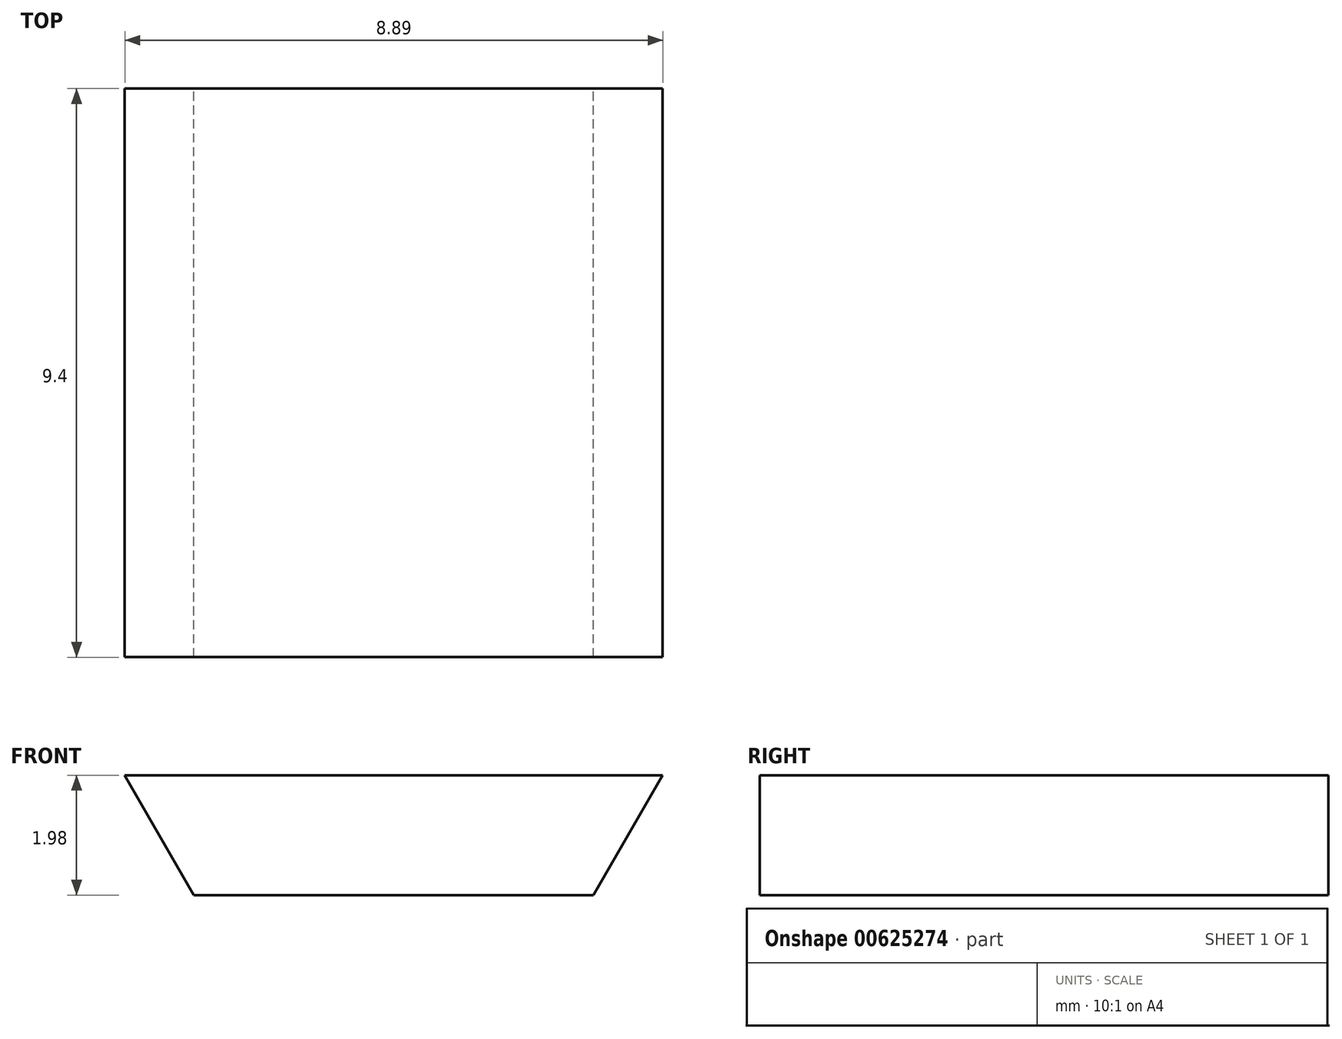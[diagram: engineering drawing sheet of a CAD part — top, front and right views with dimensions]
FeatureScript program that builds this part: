
annotation { "Feature Type Name" : "Feature", "Feature Type Description" : "" }
export const myFeature = defineFeature(function(context is Context, id is Id, definition is map)
    precondition{}
    {
        {
            var Q0;
            Q0=qCreatedBy(makeId("Front.planeOp"),FACE);
            var sketch = newSketch(context, id + "F0", { "sketchPlane" : qUnion([Q0])});
            skLineSegment(sketch, "E0", {"start": v(2.85, 0) * mm, "end": v(-3.75, 0) * mm});
            skLineSegment(sketch, "E1", {"start": v(-3.75, 0) * mm, "end": v(-4.9, 1.98) * mm});
            skLineSegment(sketch, "E2", {"start": v(-4.9, 1.98) * mm, "end": v(4, 1.98) * mm});
            skLineSegment(sketch, "E3", {"start": v(4, 1.98) * mm, "end": v(2.85, 0) * mm});
            skSolve(sketch);
        }
        {
            var Q0;
            Q0=makeQuery(id+"F0.imprint","IMPRINT",FACE,{"disambiguationData":[TD([[makeQuery(id+"F0.imprint","IMPRINT",EDGE,{"derivedFrom":sQuery(id+"F0.wireOp",EDGE,"E0")}),-1.0]])]});
            extrude(context, id + "F1", {"entities" : qUnion([Q0]), "depth" : 9.4 * mm, "offsetDistance" : 25.4 * mm});
        }
    });
